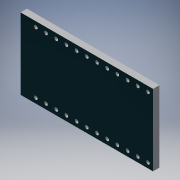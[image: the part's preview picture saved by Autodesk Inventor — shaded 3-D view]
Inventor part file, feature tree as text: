
AUTODESK INVENTOR PART (.ipt)
format: ipt  version: 2018 (Build 220112000, 112)  size: 293,376 bytes
history: native  units: mm
features: other x5, extrude x3, sketch x3, projected_geometry x3, chamfer x1, fillet x1, pattern_linear x1, reference x1
ambient origin geometry x8: Origin, YZ Plane, XZ Plane, XY Plane, X Axis, Y Axis, Z Axis, Center Point
bodies: Volumenkörper1 (feature_tree)
feature tree (18):
  extrude  "Extrusion1"  Depth=1.5mm TaperAngle=0.0deg
  extrude  "Extrusion2"  Depth=0.15mm TaperAngle=45.0deg
  extrude  "Extrusion3"  Depth=120.0mm
  chamfer  "Fase1"  Distance=20.0mm
  fillet  "Rundung1"  [1 undecoded]
  pattern_linear  "Rechteckige Anordnung1"  [2 undecoded]
  sketch  "Skizze1"  dims[d0=10.0mm d1=0.0mm d2=1.5mm d3=0.0mm]
  projected_geometry  "Projizierte Kontur1"
  sketch  "Skizze2"  dims[d4=0.25mm d5=0.0mm d6=0.15mm d7=1.5mm d8=45.0deg]
  projected_geometry  "Projizierte Kontur2"
  reference  "Referenz1"
  sketch  "Skizze3"  dims[d9=0.25mm d10=120.0mm d12=2.54mm d13=20.0mm d15=15.25mm]
  projected_geometry  "Projizierte Kontur3"
  other  "LPattern2"
  parser-record x1  (decoder bookkeeping rows leaked as tree rows — omitted from the tree; the rows remain in map.json)
  other  "ARDUINO PRO MICRO.iam"
  other  "MICRO_stackable header 12_2"
  other  "MICRO_stackable header pin_36"
note: 3 required parameter values undecoded (feature->parameter linkage not recoverable at this tier; creation-order binding heuristic only, values carry confidence <= 0.55)
note: 1 file-system path scrubbed to <path> (originals preserved in map.json)
